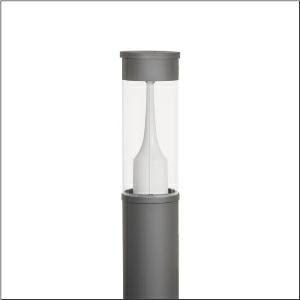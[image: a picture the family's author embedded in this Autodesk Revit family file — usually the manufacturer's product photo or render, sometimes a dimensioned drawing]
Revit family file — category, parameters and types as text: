
# Revit family: city-light_260_iq___st1_2a_5xa5295mf14h_84f0
name_source: partatom
category: Lighting Fixtures
units: mm (PartAtom-declared; Revit-internal decimal feet)

## family parameters
Cut with Voids When Loaded = No
Host = Face
Light Source = No
Part Type = Normal
Room Calculation Point = No
Round Connector Dimension = Use Diameter
Shared = No

## types (1)
- --- (1 x LED, 1540 lm, 11.8 W, 2700K)
    Apparent Load = 12 VA
    CIE Flux Codes = 22 61 93 96 100
    Color Rendering = 70
    Color Temperature = 2700K
    Default Elevation = 1800 mm
    Description = City-Light 260 iQ, light pillar, Module 540 iQ-SR, primary light control with 3 zone facetted reflector, of plastic, silver coated, highly specular, structured, primary optical cover: cover, of PMMA, transparent, partly coated, light distribution: ST1.2a, primary light characteristic: asymmetric, LED, High Power LED, rated luminous flux: 1.540lm, luminous efficacy: 131lm/W, light colour: 727, colour temperature: 2700K, control gear: ECG iQ, control: presetting dimming logarithmic, Street-Remote, Auto-Match, Temp-Guard, Lumen-Switch, Night-Set, Smart-Wire, Light-Fading, Desk-Remote (wireless, voltage-free reading and setting of iQ features in the workshop via application-optimized NFC function/RFID function), optimised constant luminous flux control (CLO 2.0), with terminal, 6-pole, max. 2.5mm², mains connection: 230..240V, AC, 50/60Hz, start of lifetime: 12W, end of service life: 12W, reduction: 6W, luminaire housing, cylindrical, of extruded aluminium section, coated, Siteco® metallic grey (DB 702S), length: 2.600mm, diameter: 200mm, Module 540 iQ-SR, traffic white (RAL 9016), equipment: standard, protection rating (complete): IP65, insulation class (complete): insulation class II (safety insulation), certification: CE, ENEC, VDE, packaging unit: 1 piece

Light Distribution: ST1.2a
    Height = 500 mm
    Lamp = 1 x LED
    Lamp Light Flux = 1540 lm
    Lamp Power = 11.8 W
    Lamp count = 1
    Length = 200 mm  [stored 0.656168 ft]
    Luminous efficacy = 131 lm/W
    Manufacturer = Siteco
    ModVariant = No
    Model = 5XA5295MF14H
    Mounting Place = Floor
    Mounting Type = Freestanding
    Number of Poles = 1
    OnlyDefault = Yes
    Power Factor = 1
    Product Name = City-Light 260 iQ | ST1.2a
    Product group = light pillar
    ProductGroupID = 1303
    Protection Class = Protection class II
    Protection Degree = IP 65
    RLX_Detail_Level = 1
    RLX_Emergency_Light_Flux = 0 lm
    RLX_Emergency_Type = 0
    RLX_Emergency_Type_DB = No
    RlxData = <blob elided: 60681 chars, md5=059bf508>
    Socket = socket
    Standby Power = 0 W
    System Light Flux = 1540 lm
    System Power = 12 W
    Type Comments = factory setting: luminous flux: 100 % | dim-lin: 254 | 472 mA
    Type Image = l_1006918.jpg
    URL = http://relux.com
    VarID = @adj_103243
    Voltage = 0 V
    Weight = 0.00 kg
    Width = 0 mm  [stored 0 ft]

note: [stored X ft] marks values corroborated as IEEE doubles in the binary element streams (Revit-internal decimal feet)

## geometry (parser evidence)
native form markers: Blend x4, Sweep x13
no freeform markers — native parametric forms only
